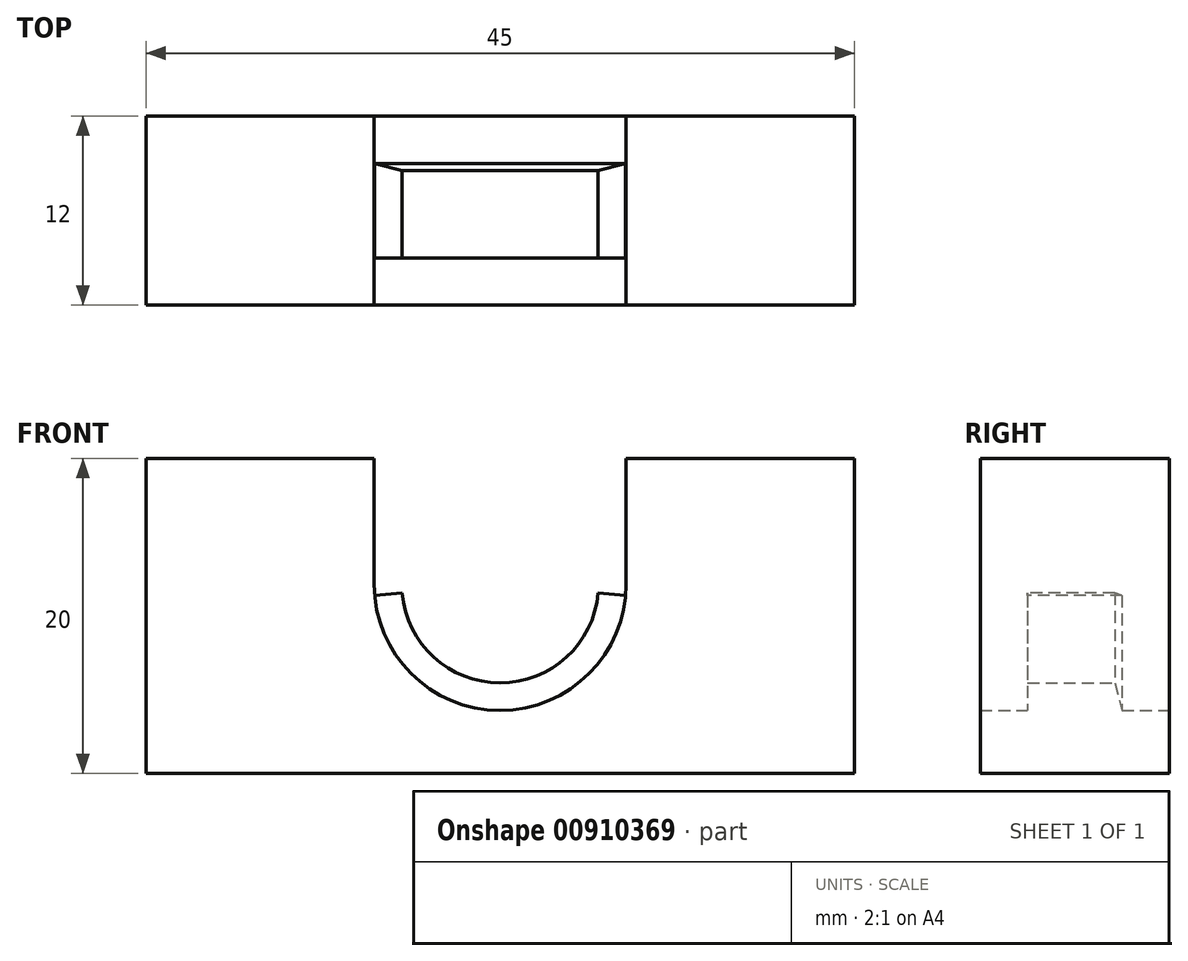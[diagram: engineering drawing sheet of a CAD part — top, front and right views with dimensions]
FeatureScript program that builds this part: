
annotation { "Feature Type Name" : "Feature", "Feature Type Description" : "" }
export const myFeature = defineFeature(function(context is Context, id is Id, definition is map)
    precondition{}
    {
        {
            var Q0;
            Q0=qCreatedBy(makeId("Top.planeOp"),FACE);
            var sketch = newSketch(context, id + "F0", { "sketchPlane" : qUnion([Q0])});
            skLineSegment(sketch, "E0.bottom", {"start": v(-22.5, 0) * mm, "end": v(22.5, 0) * mm});
            skLineSegment(sketch, "E0.top", {"start": v(-22.5, 12) * mm, "end": v(22.5, 12) * mm});
            skLineSegment(sketch, "E0.left", {"start": v(-22.5, 0) * mm, "end": v(-22.5, 12) * mm});
            skLineSegment(sketch, "E0.right", {"start": v(22.5, 0) * mm, "end": v(22.5, 12) * mm});
            skSolve(sketch);
        }
        {
            var Q0;
            Q0 = qSketchRegion(id + "F0", true);
            extrude(context, id + "F1", {"entities" : qUnion([Q0]), "depth" : 20 * mm, "offsetDistance" : 25.4 * mm});
        }
        {
            var Q0;
            Q0=makeQuery(id+"F1.opExtrude","SWEPT_FACE",FACE,{"disambiguationData":[OSD([sQuery(id+"F0.wireOp",EDGE,"E0.top")])]});
            var sketch = newSketch(context, id + "F2", { "sketchPlane" : qUnion([Q0])});
            skLineSegment(sketch, "E1", {"start": v(8, 12) * mm, "end": v(8, 20) * mm});
            skLineSegment(sketch, "E2", {"start": v(8, 20) * mm, "end": v(-8, 20) * mm});
            skLineSegment(sketch, "E3", {"start": v(-8, 20) * mm, "end": v(-8, 12) * mm});
            skArc(sketch, "E4", {"start": v(-8, 12) * mm, "mid": v(0, 4) * mm, "end": v(8, 12) * mm});
            skSolve(sketch);
        }
        {
            var Q0;
            Q0 = qSketchRegion(id + "F2", true);
            extrude(context, id + "F3", {"entities" : qUnion([Q0]), "operationType" : NewBodyOperationType.REMOVE, "endBound" : BoundingType.THROUGH_ALL, "oppositeDirection" : true, "depth" : 25.4 * mm, "offsetDistance" : 25.4 * mm});
        }
        {
            var Q0;
            Q0=qCreatedBy(makeId("Right.planeOp"),FACE);
            var sketch = newSketch(context, id + "F4", { "sketchPlane" : qUnion([Q0])});
            skLineSegment(sketch, "E5.0", {"start": v(12, 12) * mm, "end": v(12, 4) * mm, "construction": true});
            skLineSegment(sketch, "E5.1", {"start": v(0, 12) * mm, "end": v(0, 4) * mm, "construction": true});
            skLineSegment(sketch, "E6", {"start": v(12, 4) * mm, "end": v(0, 4) * mm, "construction": true});
            skLineSegment(sketch, "E7.bottom", {"start": v(9, 4) * mm, "end": v(3, 4) * mm});
            skLineSegment(sketch, "E7.top", {"start": v(8.53, 5.75) * mm, "end": v(3, 5.75) * mm});
            skLineSegment(sketch, "E7.left", {"start": v(9, 4) * mm, "end": v(8.53, 5.75) * mm});
            skLineSegment(sketch, "E7.right", {"start": v(3, 4) * mm, "end": v(3, 5.75) * mm});
            skLineSegment(sketch, "E8", {"start": v(12, 12) * mm, "end": v(0, 12) * mm, "construction": true});
            skSolve(sketch);
        }
        {
            var Q0;
            Q0 = qSketchRegion(id + "F4", true);
            var Q1;
            Q1=sQuery(id+"F4.wireOp",EDGE,"E8");
            revolve(context, id + "F5", {"operationType" : NewBodyOperationType.ADD, "surfaceOperationType" : NewSurfaceOperationType.NEW, "entities" : qUnion([Q0]), "axis" : qUnion([Q1]), "revolveType" : RevolveType.TWO_DIRECTIONS, "angle" : 85 * degree, "angleBack" : 275 * degree});
        }
    });
